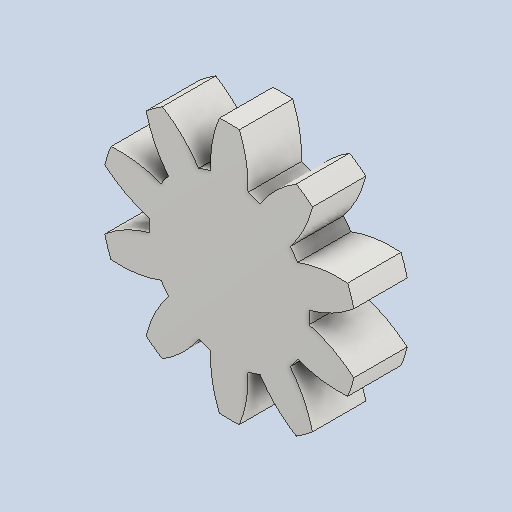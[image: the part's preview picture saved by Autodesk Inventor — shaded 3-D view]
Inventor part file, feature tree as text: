
AUTODESK INVENTOR PART (.ipt)
format: ipt  version: 2024 (Build 280153000, 153)  size: 193,536 bytes
history: native  units: mm (DEFAULTED — no unit token found)
features: plane x3, other x3, extrude x1, sketch x1
ambient origin geometry x8: Origin, YZ Plane, XZ Plane, XY Plane, X Axis, Y Axis, Z Axis, Center Point
bodies: Solid1 (feature_tree)
feature tree (8):
  extrude  "Extrusion1"  Depth=5.0mm TaperAngle=0.0deg
  plane  "Work Plane2"
  plane  "Work Plane8"
  plane  "Work Plane9"
  other  "Spur Gear"
  sketch  "Sketch1"  dims[d0=24.0mm d1=5.0mm d2=0.0mm d3=20.0mm d4=10.0mm d5=0.0mm d16=35.0mm d17=0.0mm d34=3.141593mm d39=0.0mm d41=0.0mm d43=35.0mm d46=35.0mm d47=0.0mm d48=0.0mm]
  other  "Srf1"
  other  "Pitch Diameter"
